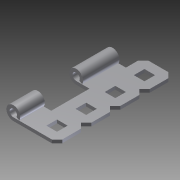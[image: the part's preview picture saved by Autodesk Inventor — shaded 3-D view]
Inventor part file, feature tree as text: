
AUTODESK INVENTOR PART (.ipt)
format: ipt  version: 2012 (Build 160160000, 160)  size: 111,104 bytes
history: native  units: in
note: dims shown in document units (in); Inventor stores cm internally (conversion verified against a paired STEP export)
features: other x2, plane x1, split x1, imported_body x1
ambient origin geometry x8: Origin, YZ Plane, XZ Plane, XY Plane, X Axis, Y Axis, Z Axis, Center Point
feature tree (5):
  other  "Cut-Extrude3"
  other  "VEX-HINGE-2 RevA1"
  plane  "Work Plane1"
  split  "Split1"
  imported_body  "Base1"
